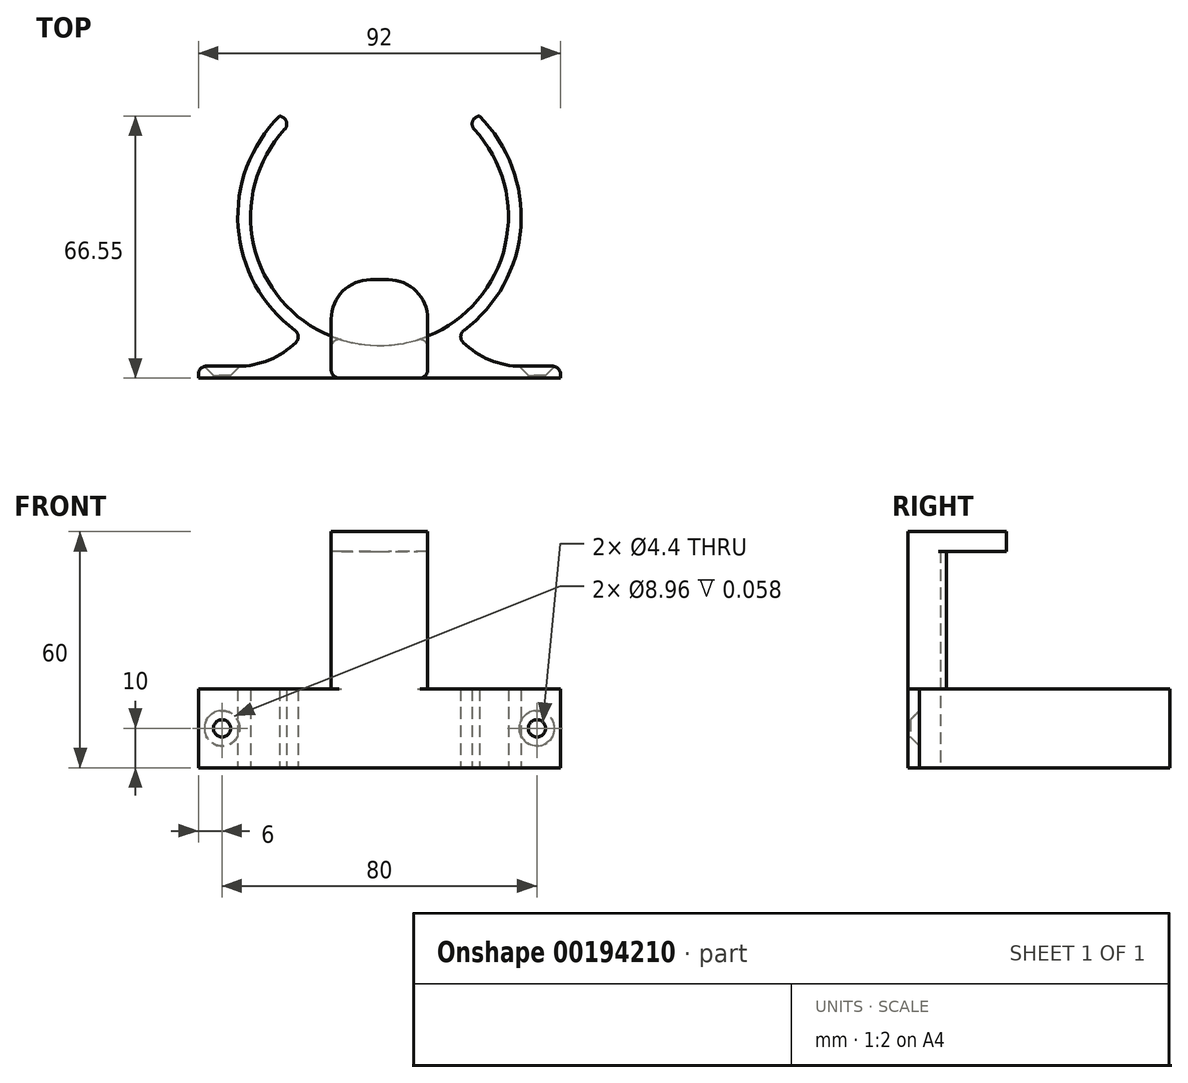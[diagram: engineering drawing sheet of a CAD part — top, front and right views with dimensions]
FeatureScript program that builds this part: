
annotation { "Feature Type Name" : "Feature", "Feature Type Description" : "" }
export const myFeature = defineFeature(function(context is Context, id is Id, definition is map)
    precondition{}
    {
        {
            assignVariable(context, id + "F0", {"name" : "h", "anyValue" : 20});
        }
        {
            var Q0;
            Q0=qCreatedBy(makeId("Top.planeOp"),FACE);
            var sketch = newSketch(context, id + "F1", { "sketchPlane" : qUnion([Q0])});
            skCircle(sketch, "E0", {"center": v(0, 0) * mm, "radius": 36 * mm});
            skCircle(sketch, "E1", {"center": v(0, 0) * mm, "radius": 32.75 * mm});
            skLineSegment(sketch, "E2", {"start": v(-36, 0) * mm, "end": v(36, 0) * mm, "construction": true});
            skLineSegment(sketch, "E3", {"start": v(36, 0) * mm, "end": v(36, -41) * mm});
            skLineSegment(sketch, "E4", {"start": v(36, -41) * mm, "end": v(-36, -41) * mm});
            skLineSegment(sketch, "E5", {"start": v(-36, -41) * mm, "end": v(-36, 0) * mm});
            skLineSegment(sketch, "E6", {"start": v(-36, -41) * mm, "end": v(-46, -41) * mm});
            skLineSegment(sketch, "E7", {"start": v(-46, -41) * mm, "end": v(-46, -38) * mm});
            skLineSegment(sketch, "E8", {"start": v(-46, -38) * mm, "end": v(-36, -38) * mm});
            skLineSegment(sketch, "E9", {"start": v(36, -41) * mm, "end": v(46, -41) * mm});
            skLineSegment(sketch, "E10", {"start": v(46, -41) * mm, "end": v(46, -38) * mm});
            skLineSegment(sketch, "E11", {"start": v(46, -38) * mm, "end": v(36, -38) * mm});
            skLineSegment(sketch, "E12", {"start": v(-36, -17.01) * mm, "end": v(36, -17.01) * mm, "construction": true});
            skCircle(sketch, "E13", {"center": v(-36, -17.01) * mm, "radius": 20.99 * mm});
            skCircle(sketch, "E14", {"center": v(36, -17.01) * mm, "radius": 20.99 * mm});
            skLineSegment(sketch, "E15", {"start": v(-25.37, 25.55) * mm, "end": v(25.37, 25.55) * mm, "construction": true});
            skLineSegment(sketch, "E16", {"start": v(-25.37, 25.55) * mm, "end": v(-20.5, 25.55) * mm});
            skLineSegment(sketch, "E17", {"start": v(25.37, 25.55) * mm, "end": v(20.5, 25.55) * mm});
            skSolve(sketch);
        }
        {
            var Q0;
            {var subQ0=sQuery(id+"F1.wireOp",EDGE,"E6");Q0=makeQuery(id+"F1.imprint","IMPRINT",FACE,{"disambiguationData":[TD([[makeQuery(id+"F1.imprint","IMPRINT",EDGE,{"derivedFrom":subQ0}),-1.0]])]});}
            var Q1;
            {var subQ1=sQuery(id+"F1.wireOp",EDGE,"E4");Q1=makeQuery(id+"F1.imprint","IMPRINT",FACE,{"disambiguationData":[TD([[makeQuery(id+"F1.imprint","IMPRINT",EDGE,{"derivedFrom":subQ1}),-1.0]])]});}
            var Q2;
            {var subQ0=sQuery(id+"F1.wireOp",EDGE,"E9");Q2=makeQuery(id+"F1.imprint","IMPRINT",FACE,{"disambiguationData":[TD([[makeQuery(id+"F1.imprint","IMPRINT",EDGE,{"derivedFrom":subQ0}),1.0]])]});}
            var Q3;
            {var subQ0=sQuery(id+"F1.wireOp",EDGE,"E13");var subQ1=sQuery(id+"F1.wireOp",EDGE,"E0");var subQ2=makeQuery(id+"F1.imprint","INTERSECT",VERTEX,{"disambiguationData":[OD(1.0)],"derivedFrom":[subQ1,subQ0]});Q3=makeQuery(id+"F1.imprint","IMPRINT",FACE,{"disambiguationData":[TD([[makeQuery(id+"F1.imprint","IMPRINT",EDGE,{"disambiguationData":[TD([[subQ2,-1.0]])],"derivedFrom":subQ1}),1.0]])]});}
            var Q4;
            {var subQ0=sQuery(id+"F1.wireOp",EDGE,"E14");var subQ1=sQuery(id+"F1.wireOp",EDGE,"E0");var subQ2=makeQuery(id+"F1.imprint","INTERSECT",VERTEX,{"disambiguationData":[OD(0.0)],"derivedFrom":[subQ1,subQ0]});Q4=makeQuery(id+"F1.imprint","IMPRINT",FACE,{"disambiguationData":[TD([[makeQuery(id+"F1.imprint","IMPRINT",EDGE,{"disambiguationData":[TD([[subQ2,-1.0]])],"derivedFrom":subQ1}),1.0]])]});}
            var Q5;
            {var subQ5=sQuery(id+"F1.wireOp",EDGE,"E0");var subQ6=makeQuery(id+"F1.imprint","INTERSECT",VERTEX,{"derivedFrom":[subQ5,sQuery(id+"F1.wireOp",EDGE,"E3")]});Q5=makeQuery(id+"F1.imprint","IMPRINT",FACE,{"disambiguationData":[TD([[makeQuery(id+"F1.imprint","IMPRINT",EDGE,{"disambiguationData":[TD([[subQ6,-1.0]])],"derivedFrom":subQ5}),1.0]])]});}
            var Q6;
            {var subQ0=sQuery(id+"F1.wireOp",EDGE,"E13");var subQ1=sQuery(id+"F1.wireOp",EDGE,"E0");var subQ2=makeQuery(id+"F1.imprint","INTERSECT",VERTEX,{"disambiguationData":[OD(0.0)],"derivedFrom":[subQ1,subQ0]});Q6=makeQuery(id+"F1.imprint","IMPRINT",FACE,{"disambiguationData":[TD([[makeQuery(id+"F1.imprint","IMPRINT",EDGE,{"disambiguationData":[TD([[subQ2,-1.0]])],"derivedFrom":subQ1}),1.0]])]});}
            var Q7;
            {var subQ5=sQuery(id+"F1.wireOp",EDGE,"E16");Q7=makeQuery(id+"F1.imprint","IMPRINT",FACE,{"disambiguationData":[TD([[makeQuery(id+"F1.imprint","IMPRINT",EDGE,{"derivedFrom":subQ5}),-1.0]])]});}
            extrude(context, id + "F2", {"entities" : qUnion([Q0, Q1, Q2, Q3, Q4, Q5, Q6, Q7]), "depth" : (getVariable(context, 'h')) * mm});
        }
        {
            var Q0;
            Q0=makeQuery(id+"F2.opExtrude","SWEPT_EDGE",EDGE,{"disambiguationData":[OSD([sQuery(id+"F1.wireOp",EDGE,"E1"),sQuery(id+"F1.wireOp",EDGE,"E17")])]});
            var Q1;
            Q1=makeQuery(id+"F2.opExtrude","SWEPT_EDGE",EDGE,{"disambiguationData":[OSD([sQuery(id+"F1.wireOp",EDGE,"E1"),sQuery(id+"F1.wireOp",EDGE,"E16")])]});
            var Q2;
            Q2=makeQuery(id+"F2.opExtrude","SWEPT_EDGE",EDGE,{"disambiguationData":[OSD([sQuery(id+"F1.wireOp",EDGE,"E0"),sQuery(id+"F1.wireOp",EDGE,"E13")])]});
            var Q3;
            Q3=makeQuery(id+"F2.opExtrude","SWEPT_EDGE",EDGE,{"disambiguationData":[OSD([sQuery(id+"F1.wireOp",EDGE,"E0"),sQuery(id+"F1.wireOp",EDGE,"E14")])]});
            var Q4;
            Q4=makeQuery(id+"F2.opExtrude","SWEPT_EDGE",EDGE,{"disambiguationData":[OSD([sQuery(id+"F1.wireOp",EDGE,"E10"),sQuery(id+"F1.wireOp",EDGE,"E11")])]});
            var Q5;
            Q5=makeQuery(id+"F2.opExtrude","SWEPT_EDGE",EDGE,{"disambiguationData":[OSD([sQuery(id+"F1.wireOp",EDGE,"E7"),sQuery(id+"F1.wireOp",EDGE,"E8")])]});
            fillet(context, id + "F3", {"entities" : qUnion([Q0, Q1, Q2, Q3, Q4, Q5]), "radius" : 2 * mm, "tangentPropagation" : true, "allowEdgeOverflow" : false});
        }
        {
            var Q0;
            Q0=makeQuery(id+"F2.opExtrude","SWEPT_FACE",FACE,{"disambiguationData":[OSD([sQuery(id+"F1.wireOp",EDGE,"E11")])]});
            var sketch = newSketch(context, id + "F4", { "sketchPlane" : qUnion([Q0])});
            skLineSegment(sketch, "E18", {"start": v(-44, 10) * mm, "end": v(17, 10) * mm, "construction": true});
            skPoint(sketch, "E19", {"position": v(-40, 10) * mm});
            skPoint(sketch, "E20", {"position": v(40, 10) * mm});
            skSolve(sketch);
        }
        {
            var Q0;
            Q0=sQuery(id+"F4.wireOp",VERTEX,"E20");
            var Q1;
            Q1=sQuery(id+"F4.wireOp",VERTEX,"E19");
            var Q2;
            Q2=makeQuery(id+"F2.opExtrude","SWEPT_BODY",BODY,{"disambiguationData":[OSD([sQuery(id+"F1.wireOp",EDGE,"E0"),sQuery(id+"F1.wireOp",EDGE,"E1"),sQuery(id+"F1.wireOp",EDGE,"E4"),sQuery(id+"F1.wireOp",EDGE,"E6"),sQuery(id+"F1.wireOp",EDGE,"E7"),sQuery(id+"F1.wireOp",EDGE,"E8"),sQuery(id+"F1.wireOp",EDGE,"E9"),sQuery(id+"F1.wireOp",EDGE,"E10"),sQuery(id+"F1.wireOp",EDGE,"E11"),sQuery(id+"F1.wireOp",EDGE,"E13"),sQuery(id+"F1.wireOp",EDGE,"E14"),sQuery(id+"F1.wireOp",EDGE,"E16"),sQuery(id+"F1.wireOp",EDGE,"E17")])]});
            hole(context, id + "F5", {"style" : HoleStyle.C_SINK, "endStyle" : HoleEndStyle.BLIND, "standardTappedOrClearance" : lookupTablePath({ "standard" : "ISO", "fit" : "Normal", "size" : "M4", "type" : "Clearance" }), "standardBlindInLast" : lookupTablePath({ "fit" : "Standard", "standard" : "ISO", "size" : "M4", "type" : "Clearance" }), "holeDiameter" : 4.4 * mm, "cSinkDiameter" : 8.96 * mm, "cSinkAngle" : 90 * degree, "holeDepth" : 12 * mm, "locations" : qUnion([Q0, Q1]), "scope" : qUnion([Q2])});
        }
        {
            var Q0;
            Q0=makeQuery(id+"F2.opExtrude","CAP_FACE",FACE,{"disambiguationData":[OSD([sQuery(id+"F1.wireOp",EDGE,"E0"),sQuery(id+"F1.wireOp",EDGE,"E1"),sQuery(id+"F1.wireOp",EDGE,"E4"),sQuery(id+"F1.wireOp",EDGE,"E6"),sQuery(id+"F1.wireOp",EDGE,"E7"),sQuery(id+"F1.wireOp",EDGE,"E8"),sQuery(id+"F1.wireOp",EDGE,"E9"),sQuery(id+"F1.wireOp",EDGE,"E10"),sQuery(id+"F1.wireOp",EDGE,"E11"),sQuery(id+"F1.wireOp",EDGE,"E13"),sQuery(id+"F1.wireOp",EDGE,"E14"),sQuery(id+"F1.wireOp",EDGE,"E16"),sQuery(id+"F1.wireOp",EDGE,"E17")])],"isStart":false});
            var sketch = newSketch(context, id + "F6", { "sketchPlane" : qUnion([Q0])});
            skLineSegment(sketch, "E21", {"start": v(-12.25, -30.37) * mm, "end": v(-12.25, -41) * mm});
            skPoint(sketch, "E21.startSnap0", {"position": v(-20.65, -30.37) * mm});
            skPoint(sketch, "E22.endSnap0", {"position": v(20.65, -30.37) * mm});
            skLineSegment(sketch, "E23", {"start": v(12.25, -30.37) * mm, "end": v(12.25, -41) * mm});
            skLineSegment(sketch, "E24", {"start": v(12.25, -41) * mm, "end": v(-12.25, -41) * mm});
            skSolve(sketch);
        }
        {
            var Q0;
            {var subQ0=sQuery(id+"F6.wireOp",EDGE,"E21");Q0=makeQuery(id+"F6.imprint","IMPRINT",FACE,{"disambiguationData":[TD([[makeQuery(id+"F6.imprint","IMPRINT",EDGE,{"derivedFrom":subQ0}),1.0]])]});}
            extrude(context, id + "F7", {"entities" : qUnion([Q0]), "operationType" : NewBodyOperationType.ADD, "depth" : 35 * mm});
        }
        {
            var Q0;
            Q0=makeQuery(id+"F7.opExtrude","CAP_FACE",FACE,{"disambiguationData":[OSD([sQuery(id+"F1.wireOp",EDGE,"E1"),sQuery(id+"F6.wireOp",EDGE,"E21"),sQuery(id+"F6.wireOp",EDGE,"E23"),sQuery(id+"F6.wireOp",EDGE,"E24")])],"isStart":false});
            var sketch = newSketch(context, id + "F8", { "sketchPlane" : qUnion([Q0])});
            skLineSegment(sketch, "E25", {"start": v(-12.25, -41) * mm, "end": v(-12.25, -16) * mm});
            skLineSegment(sketch, "E26", {"start": v(-12.25, -16) * mm, "end": v(12.25, -16) * mm});
            skLineSegment(sketch, "E27", {"start": v(12.25, -16) * mm, "end": v(12.25, -41) * mm});
            skLineSegment(sketch, "E28", {"start": v(12.25, -41) * mm, "end": v(-12.25, -41) * mm});
            skSolve(sketch);
        }
        {
            var Q0;
            {var subQ2=sQuery(id+"F8.wireOp",EDGE,"E26");Q0=makeQuery(id+"F8.imprint","IMPRINT",FACE,{"disambiguationData":[TD([[makeQuery(id+"F8.imprint","IMPRINT",EDGE,{"derivedFrom":subQ2}),-1.0]])]});}
            var Q1;
            {var subQ2=sQuery(id+"F8.wireOp",EDGE,"E28");Q1=makeQuery(id+"F8.imprint","IMPRINT",FACE,{"disambiguationData":[TD([[makeQuery(id+"F8.imprint","IMPRINT",EDGE,{"derivedFrom":subQ2}),-1.0]])]});}
            extrude(context, id + "F9", {"entities" : qUnion([Q0, Q1]), "operationType" : NewBodyOperationType.ADD, "depth" : 5 * mm});
        }
        {
            var Q0;
            Q0=makeQuery(id+"F7.opExtrude","SWEPT_EDGE",EDGE,{"disambiguationData":[OSD([sQuery(id+"F1.wireOp",EDGE,"E4"),sQuery(id+"F1.wireOp",EDGE,"E6"),sQuery(id+"F1.wireOp",EDGE,"E9"),sQuery(id+"F6.wireOp",EDGE,"E21"),sQuery(id+"F6.wireOp",EDGE,"E24")])]});
            var Q1;
            Q1=makeQuery(id+"F7.opExtrude","SWEPT_EDGE",EDGE,{"disambiguationData":[OSD([sQuery(id+"F1.wireOp",EDGE,"E1"),sQuery(id+"F6.wireOp",EDGE,"E21")])]});
            var Q2;
            Q2=makeQuery(id+"F7.opExtrude","SWEPT_EDGE",EDGE,{"disambiguationData":[OSD([sQuery(id+"F1.wireOp",EDGE,"E4"),sQuery(id+"F1.wireOp",EDGE,"E6"),sQuery(id+"F1.wireOp",EDGE,"E9"),sQuery(id+"F6.wireOp",EDGE,"E23"),sQuery(id+"F6.wireOp",EDGE,"E24")])]});
            var Q3;
            Q3=makeQuery(id+"F7.opExtrude","SWEPT_EDGE",EDGE,{"disambiguationData":[OSD([sQuery(id+"F1.wireOp",EDGE,"E1"),sQuery(id+"F6.wireOp",EDGE,"E23")])]});
            fillet(context, id + "F10", {"entities" : qUnion([Q0, Q1, Q2, Q3]), "radius" : 2 * mm, "tangentPropagation" : true, "allowEdgeOverflow" : false});
        }
        {
            var Q0;
            Q0=makeQuery(id+"F9.opExtrude","SWEPT_EDGE",EDGE,{"disambiguationData":[OSD([sQuery(id+"F8.wireOp",EDGE,"E26"),sQuery(id+"F8.wireOp",EDGE,"E27")])]});
            var Q1;
            Q1=makeQuery(id+"F9.opExtrude","SWEPT_EDGE",EDGE,{"disambiguationData":[OSD([sQuery(id+"F8.wireOp",EDGE,"E25"),sQuery(id+"F8.wireOp",EDGE,"E26")])]});
            fillet(context, id + "F11", {"entities" : qUnion([Q0, Q1]), "radius" : 10 * mm, "tangentPropagation" : true, "allowEdgeOverflow" : false});
        }
    });
